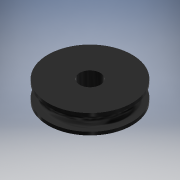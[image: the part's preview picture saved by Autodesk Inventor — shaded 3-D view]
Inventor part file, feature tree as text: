
AUTODESK INVENTOR PART (.ipt)
format: ipt  version: 2019 (Build 230136000, 136)  size: 151,040 bytes
history: native  units: in
note: dims shown in document units (in); Inventor stores cm internally (conversion verified against a paired STEP export)
features: sketch x2, revolve x1, mirror x1, extrude x1
ambient origin geometry x8: Origin, YZ Plane, XZ Plane, XY Plane, X Axis, Y Axis, Z Axis, Center Point
bodies: Solid1 (feature_tree)
feature tree (5):
  revolve  "Revolution1"  [1 undecoded]
  mirror  "Mirror1"
  extrude  "Extrusion1"  TaperAngle=90.0deg  [1 undecoded]
  sketch  "Sketch1"  dims[d2=0.0635in d4=0.0938in]
  sketch  "Sketch2"  dims[d5=0.0318in d6=90.0deg d7=0.2in d8=1.0in d9=0.0in d10=0.375in]
note: 2 required parameter values undecoded (feature->parameter linkage not recoverable at this tier; creation-order binding heuristic only, values carry confidence <= 0.55)